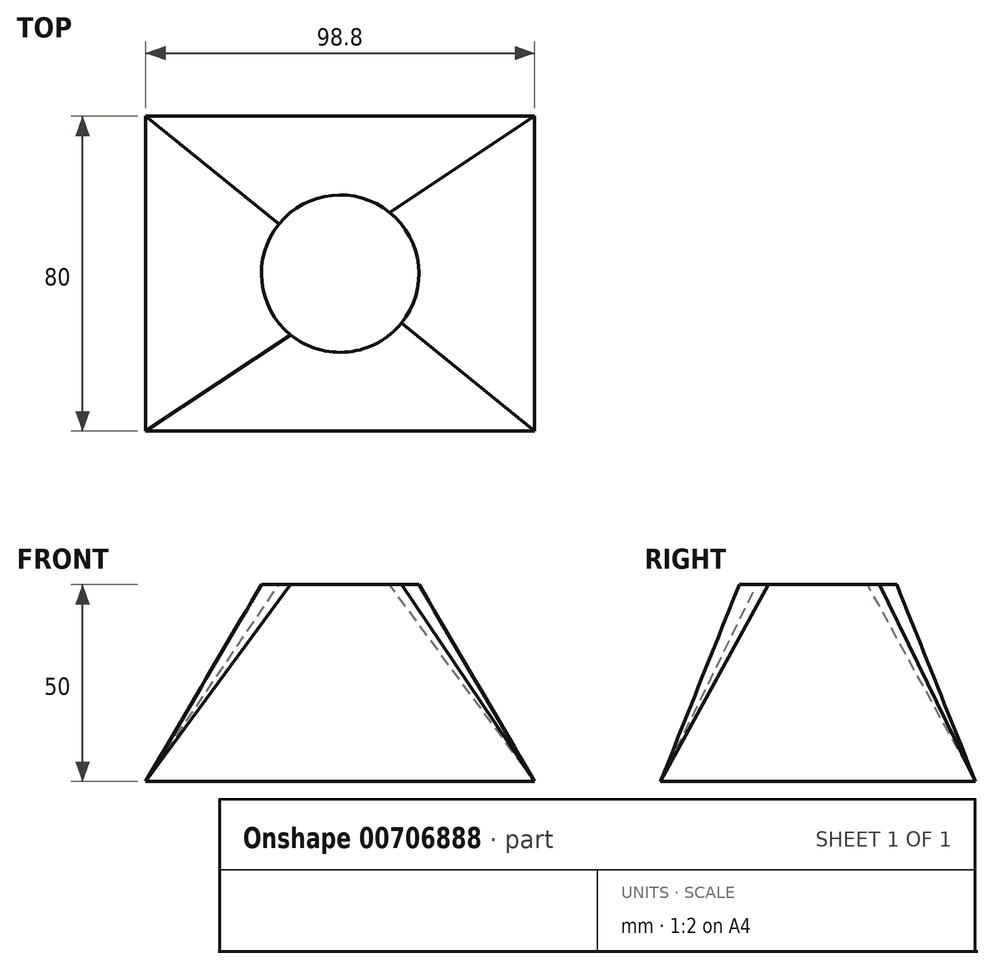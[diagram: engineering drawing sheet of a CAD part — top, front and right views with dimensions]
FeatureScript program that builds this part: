
annotation { "Feature Type Name" : "Feature", "Feature Type Description" : "" }
export const myFeature = defineFeature(function(context is Context, id is Id, definition is map)
    precondition{}
    {
        {
            var Q0;
            Q0=qCreatedBy(makeId("Top.planeOp"),FACE);
            var sketch = newSketch(context, id + "F0", { "sketchPlane" : qUnion([Q0])});
            skLineSegment(sketch, "E0.bottom", {"start": v(-49.4, 40) * mm, "end": v(49.4, 40) * mm});
            skLineSegment(sketch, "E0.top", {"start": v(-49.4, -40) * mm, "end": v(49.4, -40) * mm});
            skLineSegment(sketch, "E0.left", {"start": v(-49.4, 40) * mm, "end": v(-49.4, -40) * mm});
            skLineSegment(sketch, "E0.right", {"start": v(49.4, 40) * mm, "end": v(49.4, -40) * mm});
            skSolve(sketch);
        }
        {
            var Q0;
            Q0=qCreatedBy(makeId("Top.planeOp"),FACE);
            cPlane(context, id + "F1", {"entities" : qUnion([Q0]), "cplaneType" : CPlaneType.OFFSET, "offset" : 50 * mm, "width" : 150 * mm, "height" : 150 * mm});
        }
        {
            var Q0;
            Q0=qCreatedBy(id+"F1.planeOp",FACE);
            var sketch = newSketch(context, id + "F2", { "sketchPlane" : qUnion([Q0])});
            skCircle(sketch, "E1", {"center": v(0, 0) * mm, "radius": 20 * mm});
            skSolve(sketch);
        }
        {
            var Q0;
            Q0=makeQuery(id+"F0.imprint","IMPRINT",FACE,{"disambiguationData":[TD([[makeQuery(id+"F0.imprint","IMPRINT",EDGE,{"derivedFrom":sQuery(id+"F0.wireOp",EDGE,"E0.bottom")}),-1.0]])]});
            var Q1;
            Q1=makeQuery(id+"F2.imprint","IMPRINT",FACE,{"disambiguationData":[TD([[makeQuery(id+"F2.imprint","IMPRINT",EDGE,{"derivedFrom":sQuery(id+"F2.wireOp",EDGE,"E1")}),1.0]])]});
            loft(context, id + "F3", {"sheetProfilesArray" : [{ "sheetProfileEntities" : qUnion([Q0]) }, { "sheetProfileEntities" : qUnion([Q1]) }]});
        }
    });
